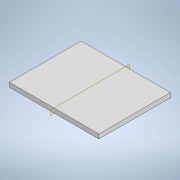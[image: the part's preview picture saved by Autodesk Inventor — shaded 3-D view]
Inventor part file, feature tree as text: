
AUTODESK INVENTOR PART (.ipt)
format: ipt  version: 2020.2 (Build 242310000, 310)  size: 102,400 bytes
history: native  units: in
note: dims shown in document units (in); Inventor stores cm internally (conversion verified against a paired STEP export)
features: extrude x1, sketch x1
ambient origin geometry x8: Origin, YZ Plane, XZ Plane, XY Plane, X Axis, Y Axis, Z Axis, Center Point
bodies: Solid1 (feature_tree)
feature tree (2):
  extrude  "Extrusion1"  Depth=4.0in
  sketch  "Sketch1"  dims[d0=0.25in d1=0.0in d3=4.0in d13=5.0in]
